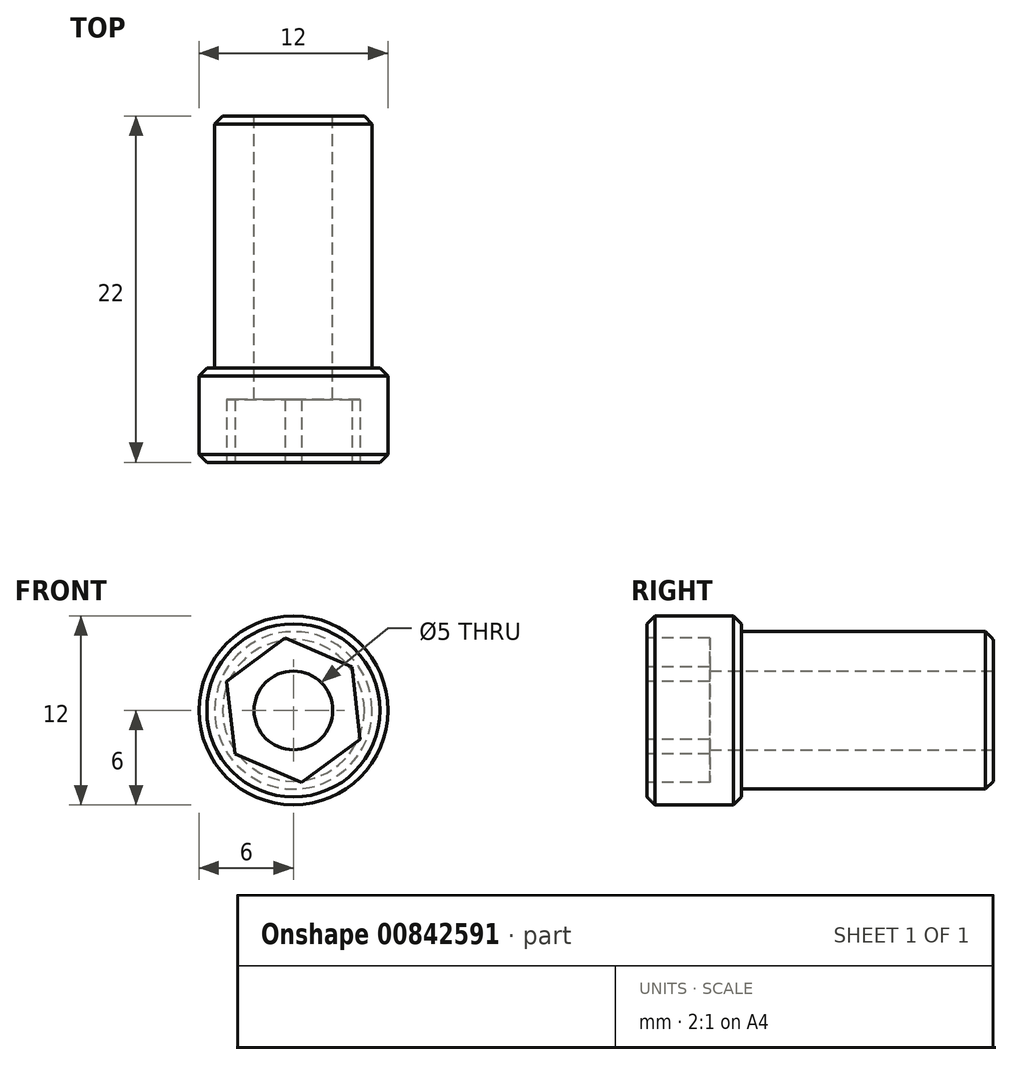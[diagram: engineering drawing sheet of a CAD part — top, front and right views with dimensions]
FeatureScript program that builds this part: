
annotation { "Feature Type Name" : "Feature", "Feature Type Description" : "" }
export const myFeature = defineFeature(function(context is Context, id is Id, definition is map)
    precondition{}
    {
        {
            var Q0;
            Q0=qCreatedBy(makeId("Front.planeOp"),FACE);
            var sketch = newSketch(context, id + "F0", { "sketchPlane" : qUnion([Q0])});
            skCircle(sketch, "E0", {"center": v(0, 0) * mm, "radius": 6 * mm});
            skSolve(sketch);
        }
        {
            var Q0;
            Q0 = qSketchRegion(id + "F0", true);
            extrude(context, id + "F1", {"entities" : qUnion([Q0]), "oppositeDirection" : true, "depth" : 6 * mm, "offsetDistance" : 25 * mm});
        }
        {
            var Q0;
            Q0=makeQuery(id+"F1.opExtrude","CAP_FACE",FACE,{"disambiguationData":[OSD([sQuery(id+"F0.wireOp",EDGE,"E0"),sQuery(id+"F0.wireOp",EDGE,"MlKOV6ic-EmtY-b1pS-uVrE-urwyClMrALkh")])],"isStart":true});
            var sketch = newSketch(context, id + "F2", { "sketchPlane" : qUnion([Q0])});
            skPoint(sketch, "E1.middle", {"position": v(0, 0) * mm});
            skPoint(sketch, "E2.right.start.orphan", {"position": v(-0.6, 7.24) * mm});
            skPoint(sketch, "E2.left.start.orphan", {"position": v(0.6, 7.24) * mm});
            skPoint(sketch, "E1.left.end.orphan", {"position": v(7.24, -0.6) * mm});
            skPoint(sketch, "E1.left.start.orphan", {"position": v(7.24, 0.6) * mm});
            skPoint(sketch, "E1.right.end.orphan", {"position": v(-7.24, -0.6) * mm});
            skPoint(sketch, "E1.right.start.orphan", {"position": v(-7.24, 0.6) * mm});
            skPoint(sketch, "E2.top.end.orphan", {"position": v(-0.6, -7.24) * mm});
            skPoint(sketch, "E2.top.start.orphan", {"position": v(0.6, -7.24) * mm});
            skCircle(sketch, "E3.cCircle", {"center": v(0, 0) * mm, "radius": 4 * mm, "construction": true});
            skLineSegment(sketch, "E3.0", {"start": v(-0.53, 4.59) * mm, "end": v(3.7, 2.75) * mm});
            skLineSegment(sketch, "E3.1", {"start": v(3.7, 2.75) * mm, "end": v(4.24, -1.83) * mm});
            skLineSegment(sketch, "E3.2", {"start": v(4.24, -1.83) * mm, "end": v(0.53, -4.59) * mm});
            skLineSegment(sketch, "E3.3", {"start": v(0.53, -4.59) * mm, "end": v(-3.7, -2.75) * mm});
            skLineSegment(sketch, "E3.4", {"start": v(-3.7, -2.75) * mm, "end": v(-4.24, 1.83) * mm});
            skLineSegment(sketch, "E3.5", {"start": v(-4.24, 1.83) * mm, "end": v(-0.53, 4.59) * mm});
            skPoint(sketch, "E3.0.midPoint", {"position": v(1.59, 3.67) * mm});
            skSolve(sketch);
        }
        {
            var Q0;
            Q0 = qSketchRegion(id + "F2", true);
            extrude(context, id + "F3", {"entities" : qUnion([Q0]), "operationType" : NewBodyOperationType.REMOVE, "oppositeDirection" : true, "depth" : 4 * mm, "offsetDistance" : 25 * mm});
        }
        {
            var Q0;
            Q0=makeQuery(id+"F1.opExtrude","CAP_FACE",FACE,{"disambiguationData":[OSD([sQuery(id+"F0.wireOp",EDGE,"E0")])],"isStart":false});
            var sketch = newSketch(context, id + "F4", { "sketchPlane" : qUnion([Q0])});
            skCircle(sketch, "E4", {"center": v(0, 0) * mm, "radius": 5 * mm});
            skSolve(sketch);
        }
        {
            var Q0;
            Q0 = qSketchRegion(id + "F4", true);
            extrude(context, id + "F5", {"entities" : qUnion([Q0]), "operationType" : NewBodyOperationType.ADD, "depth" : 16 * mm, "offsetDistance" : 25 * mm});
        }
        {
            var Q0;
            Q0=makeQuery(id+"F5.opExtrude","CAP_FACE",FACE,{"disambiguationData":[OSD([sQuery(id+"F4.wireOp",EDGE,"E4")])],"isStart":false});
            var sketch = newSketch(context, id + "F6", { "sketchPlane" : qUnion([Q0])});
            skCircle(sketch, "E5", {"center": v(0, 0) * mm, "radius": 2.5 * mm});
            skSolve(sketch);
        }
        {
            var Q0;
            Q0 = qSketchRegion(id + "F6", true);
            extrude(context, id + "F7", {"entities" : qUnion([Q0]), "operationType" : NewBodyOperationType.REMOVE, "endBound" : BoundingType.THROUGH_ALL, "oppositeDirection" : true, "depth" : 25 * mm, "offsetDistance" : 25 * mm});
        }
        {
            var Q0;
            Q0=makeQuery(id+"F1.opExtrude","CAP_EDGE",EDGE,{"disambiguationData":[OSD([sQuery(id+"F0.wireOp",EDGE,"E0")])],"isStart":true});
            var Q1;
            Q1=makeQuery(id+"F1.opExtrude","SWEPT_FACE",FACE,{"disambiguationData":[OSD([sQuery(id+"F0.wireOp",EDGE,"E0")])]});
            var Q2;
            Q2=makeQuery(id+"F5.opExtrude","CAP_EDGE",EDGE,{"disambiguationData":[OSD([sQuery(id+"F4.wireOp",EDGE,"E4")])],"isStart":false});
            chamfer(context, id + "F8", {"entities" : qUnion([Q0, Q1, Q2]), "width" : 0.5 * mm, "tangentPropagation" : true});
        }
    });
